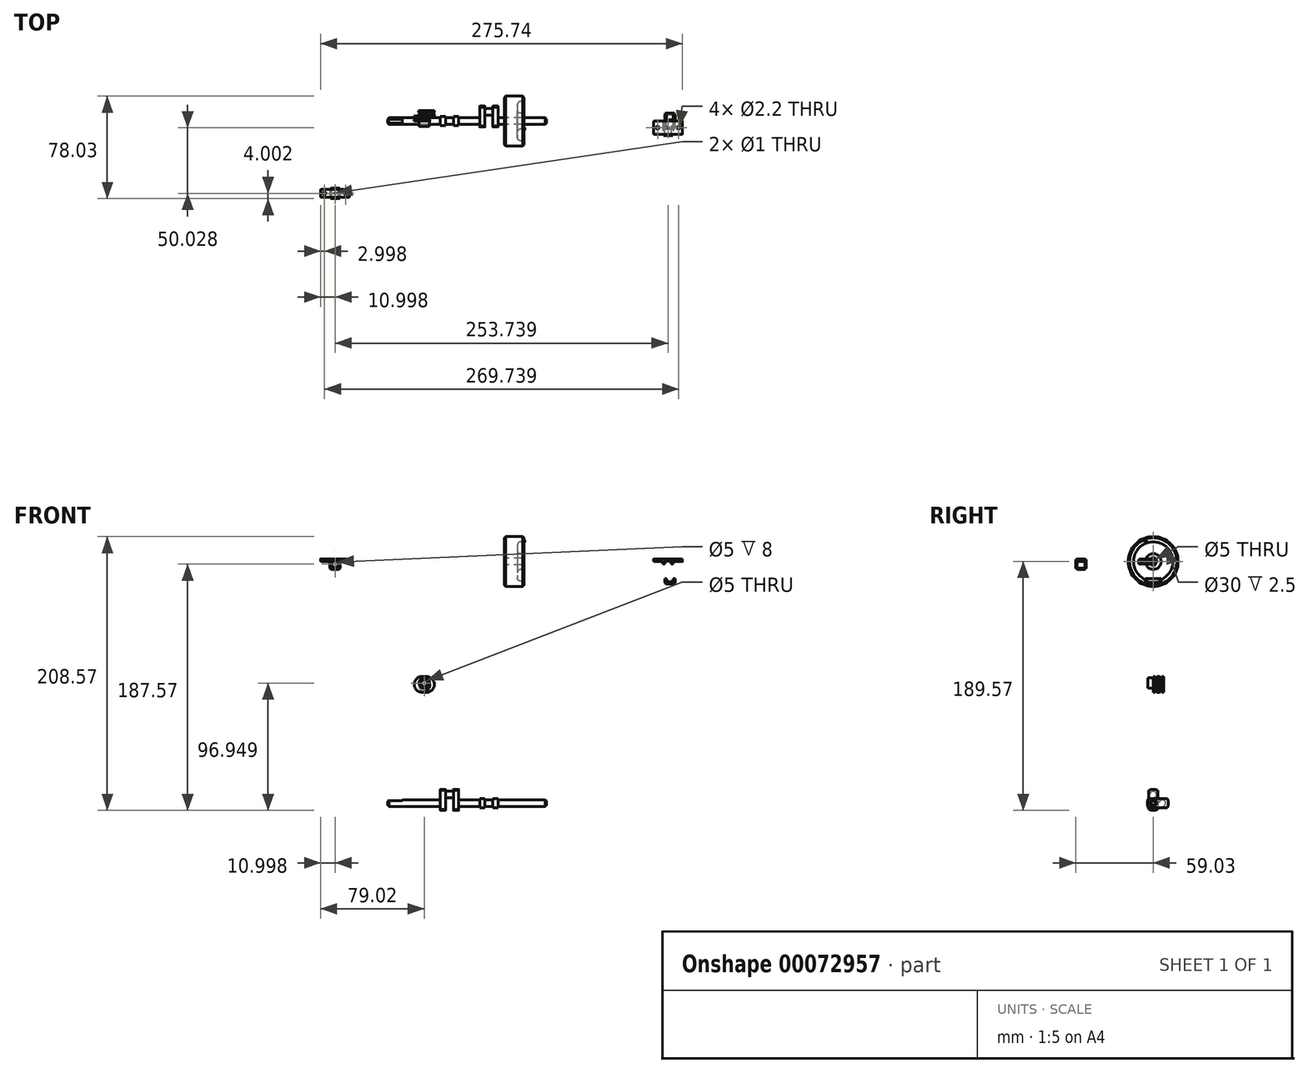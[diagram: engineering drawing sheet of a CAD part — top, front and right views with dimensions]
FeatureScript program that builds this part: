
annotation { "Feature Type Name" : "Feature", "Feature Type Description" : "" }
export const myFeature = defineFeature(function(context is Context, id is Id, definition is map)
    precondition{}
    {
        {
            var Q0;
            Q0=qCreatedBy(makeId("Front.planeOp"),FACE);
            var sketch = newSketch(context, id + "F0", { "sketchPlane" : qUnion([Q0])});
            skLineSegment(sketch, "E0", {"start": v(0, 0) * mm, "end": v(0, 2.5) * mm});
            skLineSegment(sketch, "E1", {"start": v(0, 0) * mm, "end": v(0, 19) * mm});
            skPoint(sketch, "E1.endSnap0", {"position": v(0, 1.25) * mm});
            skLineSegment(sketch, "E2", {"start": v(0, 19) * mm, "end": v(15, 19) * mm});
            skLineSegment(sketch, "E3", {"start": v(0, 19) * mm, "end": v(10, 19) * mm});
            skLineSegment(sketch, "E4", {"start": v(10, 12.5) * mm, "end": v(10, 8.5) * mm});
            skLineSegment(sketch, "E5", {"start": v(12.5, 6) * mm, "end": v(15, 6) * mm});
            skLineSegment(sketch, "E6", {"start": v(15, 19) * mm, "end": v(15, 15) * mm});
            skLineSegment(sketch, "E7", {"start": v(15, 15) * mm, "end": v(12.5, 15) * mm});
            skLineSegment(sketch, "E8", {"start": v(15, 2.5) * mm, "end": v(10, 2.5) * mm});
            skPoint(sketch, "E9.newPointB", {"position": v(10, 0) * mm});
            skArc(sketch, "E9.filletArc", {"start": v(10, 8.5) * mm, "mid": v(10.73, 6.73) * mm, "end": v(12.5, 6) * mm});
            skArc(sketch, "E10.filletArc", {"start": v(12.5, 15) * mm, "mid": v(10.73, 14.27) * mm, "end": v(10, 12.5) * mm});
            skLineSegment(sketch, "E11", {"start": v(15, 6) * mm, "end": v(15, 2.5) * mm});
            skPoint(sketch, "E12.orphan", {"position": v(16.25, 2.5) * mm});
            skLineSegment(sketch, "E13", {"start": v(0, 2.5) * mm, "end": v(15, 2.5) * mm});
            skLineSegment(sketch, "E14", {"start": v(0, 0) * mm, "end": v(10, 0) * mm});
            skSolve(sketch);
        }
        {
            var Q0;
            Q0 = qSketchRegion(id + "F0", true);
            var Q1;
            Q1=sQuery(id+"F0.wireOp",EDGE,"E14");
            revolve(context, id + "F1", {"entities" : qUnion([Q0]), "axis" : qUnion([Q1]), "revolveType" : RevolveType.FULL});
        }
        {
            var Q0;
            Q0=makeQuery(id+"F1.opRevolve","SWEPT_EDGE",EDGE,{"disambiguationData":[OSD([sQuery(id+"F0.wireOp",EDGE,"E2"),sQuery(id+"F0.wireOp",EDGE,"E6")])]});
            chamfer(context, id + "F2", {"entities" : qUnion([Q0]), "width" : 1 * mm, "tangentPropagation" : true});
        }
        {
            var Q0;
            Q0=makeQuery(id+"F1.opRevolve","SWEPT_EDGE",EDGE,{"disambiguationData":[OSD([sQuery(id+"F0.wireOp",EDGE,"E1"),sQuery(id+"F0.wireOp",EDGE,"E3")])]});
            chamfer(context, id + "F3", {"entities" : qUnion([Q0]), "width" : 1 * mm, "tangentPropagation" : true});
        }
        {
            var Q0;
            Q0=qCreatedBy(makeId("Front.planeOp"),FACE);
            var sketch = newSketch(context, id + "F4", { "sketchPlane" : qUnion([Q0])});
            skLineSegment(sketch, "E15", {"start": v(-88.77, -184.07) * mm, "end": v(-48.77, -184.07) * mm});
            skLineSegment(sketch, "E16", {"start": v(-48.77, -184.07) * mm, "end": v(-48.77, -186.57) * mm});
            skLineSegment(sketch, "E17", {"start": v(-48.77, -186.57) * mm, "end": v(-88.77, -186.57) * mm});
            skLineSegment(sketch, "E18", {"start": v(-88.77, -186.57) * mm, "end": v(-88.77, -184.07) * mm});
            skSolve(sketch);
        }
        {
            var Q0;
            Q0=makeQuery(id+"F4.imprint","IMPRINT",FACE,{"disambiguationData":[TD([[makeQuery(id+"F4.imprint","IMPRINT",EDGE,{"derivedFrom":sQuery(id+"F4.wireOp",EDGE,"E15")}),-1.0]])]});
            var Q1;
            Q1=sQuery(id+"F4.wireOp",EDGE,"E15");
            revolve(context, id + "F5", {"entities" : qUnion([Q0]), "axis" : qUnion([Q1]), "revolveType" : RevolveType.FULL});
        }
        {
            var Q0;
            Q0=makeQuery(id+"F5.opRevolve","SWEPT_FACE",FACE,{"disambiguationData":[OSD([sQuery(id+"F4.wireOp",EDGE,"E18")])]});
            var sketch = newSketch(context, id + "F6", { "sketchPlane" : qUnion([Q0])});
            skLineSegment(sketch, "E19", {"start": v(0, -184.07) * mm, "end": v(0, -182.07) * mm});
            skLineSegment(sketch, "E20", {"start": v(0, -182.07) * mm, "end": v(-1.5, -182.07) * mm});
            skLineSegment(sketch, "E21", {"start": v(-1.5, -182.07) * mm, "end": v(1.5, -182.07) * mm});
            skLineSegment(sketch, "E22", {"start": v(1.5, -182.07) * mm, "end": v(1.5, -180.36) * mm});
            skLineSegment(sketch, "E23", {"start": v(1.5, -180.36) * mm, "end": v(-1.5, -180.36) * mm});
            skLineSegment(sketch, "E24", {"start": v(-1.5, -180.36) * mm, "end": v(-1.5, -182.07) * mm});
            skSolve(sketch);
        }
        {
            var Q0;
            Q0 = qSketchRegion(id + "F6", true);
            extrude(context, id + "F7", {"entities" : qUnion([Q0]), "operationType" : NewBodyOperationType.REMOVE, "oppositeDirection" : true, "depth" : 11 * mm});
        }
        {
            var Q0;
            Q0=makeQuery(id+"F5.opRevolve","SWEPT_EDGE",EDGE,{"disambiguationData":[OSD([sQuery(id+"F4.wireOp",EDGE,"E17"),sQuery(id+"F4.wireOp",EDGE,"E18")])]});
            chamfer(context, id + "F8", {"entities" : qUnion([Q0]), "width" : 1 * mm, "tangentPropagation" : true});
        }
        {
            var Q0;
            Q0=makeQuery(id+"F5.opRevolve","SWEPT_FACE",FACE,{"disambiguationData":[OSD([sQuery(id+"F4.wireOp",EDGE,"E16")])]});
            var sketch = newSketch(context, id + "F9", { "sketchPlane" : qUnion([Q0])});
            skLineSegment(sketch, "E25", {"start": v(0, -184.07) * mm, "end": v(0, -177.57) * mm});
            skCircle(sketch, "E26", {"center": v(0, -177.57) * mm, "radius": 2.5 * mm});
            skLineSegment(sketch, "E27", {"start": v(0, -184.07) * mm, "end": v(0, -181.57) * mm});
            skLineSegment(sketch, "E28", {"start": v(0, -181.57) * mm, "end": v(3.5, -181.57) * mm});
            skArc(sketch, "E29", {"start": v(-3.5, -188.76) * mm, "mid": v(0, -189.57) * mm, "end": v(3.5, -188.76) * mm});
            skLineSegment(sketch, "E30", {"start": v(3.5, -181.57) * mm, "end": v(3.5, -184.76) * mm});
            skLineSegment(sketch, "E31", {"start": v(3.5, -184.76) * mm, "end": v(3.5, -188.76) * mm});
            skLineSegment(sketch, "E32", {"start": v(3.5, -188.76) * mm, "end": v(3.5, -174.38) * mm});
            skLineSegment(sketch, "E33.MirrorCS", {"start": v(-3.5, -188.76) * mm, "end": v(-3.5, -174.38) * mm});
            skPoint(sketch, "E34.orphan", {"position": v(3.5, -170.38) * mm});
            skArc(sketch, "E35.trimOffspring", {"start": v(3.5, -174.38) * mm, "mid": v(0, -173.57) * mm, "end": v(-3.5, -174.38) * mm});
            skPoint(sketch, "E36.MirrorCS.end.orphan", {"position": v(-3.5, -170.38) * mm});
            skSolve(sketch);
        }
        {
            var Q0;
            Q0 = qSketchRegion(id + "F9", true);
            var Q1;
            Q1=makeQuery(id+"F9.imprint","IMPRINT",FACE,{"disambiguationData":[TD([[makeQuery(id+"F9.imprint","IMPRINT",EDGE,{"derivedFrom":sQuery(id+"F9.wireOp",EDGE,"E26")}),1.0]])]});
            extrude(context, id + "F10", {"entities" : qUnion([Q0, Q1]), "operationType" : NewBodyOperationType.ADD, "depth" : 4 * mm});
        }
        {
            var Q0;
            Q0=makeQuery(id+"F9.imprint","IMPRINT",FACE,{"disambiguationData":[TD([[makeQuery(id+"F9.imprint","IMPRINT",EDGE,{"derivedFrom":sQuery(id+"F9.wireOp",EDGE,"E26")}),1.0]])]});
            extrude(context, id + "F11", {"entities" : qUnion([Q0]), "operationType" : NewBodyOperationType.ADD, "depth" : 14 * mm});
        }
        {
            var Q0;
            Q0=makeQuery(id+"F11.opExtrude","CAP_FACE",FACE,{"disambiguationData":[OSD([sQuery(id+"F9.wireOp",EDGE,"E26")])],"isStart":false});
            var sketch = newSketch(context, id + "F12", { "sketchPlane" : qUnion([Q0])});
            skLineSegment(sketch, "E37", {"start": v(0, -177.57) * mm, "end": v(0, -184.07) * mm});
            skCircle(sketch, "E38", {"center": v(0, -184.07) * mm, "radius": 2.5 * mm});
            skArc(sketch, "E39", {"start": v(-3.5, -188.76) * mm, "mid": v(0, -189.57) * mm, "end": v(3.5, -188.76) * mm});
            skLineSegment(sketch, "E40", {"start": v(0, -181.57) * mm, "end": v(3.5, -181.57) * mm});
            skLineSegment(sketch, "E41", {"start": v(3.5, -181.57) * mm, "end": v(3.5, -174.38) * mm});
            skLineSegment(sketch, "E42", {"start": v(3.5, -174.38) * mm, "end": v(3.5, -188.76) * mm});
            skLineSegment(sketch, "E43.MirrorCS", {"start": v(-3.5, -174.38) * mm, "end": v(-3.5, -188.76) * mm});
            skArc(sketch, "E44.trimOffspring", {"start": v(3.5, -174.38) * mm, "mid": v(0, -173.57) * mm, "end": v(-3.5, -174.38) * mm});
            skSolve(sketch);
        }
        {
            var Q0;
            Q0 = qSketchRegion(id + "F12", true);
            var Q1;
            Q1=makeQuery(id+"F12.imprint","IMPRINT",FACE,{"disambiguationData":[TD([[makeQuery(id+"F12.imprint","IMPRINT",EDGE,{"derivedFrom":sQuery(id+"F12.wireOp",EDGE,"E38")}),1.0]])]});
            extrude(context, id + "F13", {"entities" : qUnion([Q0, Q1]), "operationType" : NewBodyOperationType.ADD, "oppositeDirection" : true, "depth" : 4 * mm});
        }
        {
            var Q0;
            Q0=makeQuery(id+"F12.imprint","IMPRINT",FACE,{"disambiguationData":[TD([[makeQuery(id+"F12.imprint","IMPRINT",EDGE,{"derivedFrom":sQuery(id+"F12.wireOp",EDGE,"E38")}),1.0]])]});
            extrude(context, id + "F14", {"entities" : qUnion([Q0]), "operationType" : NewBodyOperationType.ADD, "depth" : 16 * mm});
        }
        {
            var Q0;
            Q0=makeQuery(id+"F14.opExtrude","CAP_FACE",FACE,{"disambiguationData":[OSD([sQuery(id+"F12.wireOp",EDGE,"E38")])],"isStart":false});
            var sketch = newSketch(context, id + "F15", { "sketchPlane" : qUnion([Q0])});
            skLineSegment(sketch, "E45", {"start": v(0, -184.07) * mm, "end": v(3.5, -184.07) * mm});
            skArc(sketch, "E46", {"start": v(-3.7, -180.57) * mm, "mid": v(-4.5, -184.07) * mm, "end": v(-3.7, -187.57) * mm});
            skLineSegment(sketch, "E47", {"start": v(3.5, -184.07) * mm, "end": v(3.5, -187.57) * mm});
            skLineSegment(sketch, "E48", {"start": v(3.5, -187.57) * mm, "end": v(10.7, -187.57) * mm});
            skLineSegment(sketch, "E49", {"start": v(10.7, -187.57) * mm, "end": v(-3.7, -187.57) * mm});
            skLineSegment(sketch, "E50.MirrorCS", {"start": v(10.7, -180.57) * mm, "end": v(-3.7, -180.57) * mm});
            skArc(sketch, "E51.trimOffspring", {"start": v(10.7, -187.57) * mm, "mid": v(11.5, -184.07) * mm, "end": v(10.7, -180.57) * mm});
            skCircle(sketch, "E52", {"center": v(0, -184.07) * mm, "radius": 2.5 * mm});
            skSolve(sketch);
        }
        {
            var Q0;
            Q0 = qSketchRegion(id + "F15", true);
            var Q1;
            Q1=makeQuery(id+"F15.imprint","IMPRINT",FACE,{"disambiguationData":[TD([[makeQuery(id+"F15.imprint","IMPRINT",EDGE,{"derivedFrom":sQuery(id+"F15.wireOp",EDGE,"E52")}),1.0]])]});
            extrude(context, id + "F16", {"entities" : qUnion([Q0, Q1]), "operationType" : NewBodyOperationType.ADD, "depth" : 4 * mm});
        }
        {
            var Q0;
            Q0=makeQuery(id+"F16.opExtrude","CAP_FACE",FACE,{"disambiguationData":[OSD([sQuery(id+"F15.wireOp",EDGE,"E46"),sQuery(id+"F15.wireOp",EDGE,"E49"),sQuery(id+"F15.wireOp",EDGE,"E50.MirrorCS"),sQuery(id+"F15.wireOp",EDGE,"E51.trimOffspring")])],"isStart":false});
            var sketch = newSketch(context, id + "F17", { "sketchPlane" : qUnion([Q0])});
            skLineSegment(sketch, "E53", {"start": v(3.5, -187.57) * mm, "end": v(3.5, -184.07) * mm});
            skLineSegment(sketch, "E54", {"start": v(3.5, -184.07) * mm, "end": v(0, -184.07) * mm});
            skCircle(sketch, "E55", {"center": v(0, -184.07) * mm, "radius": 2.5 * mm});
            skCircle(sketch, "E56.MirrorC", {"center": v(7, -184.07) * mm, "radius": 2.5 * mm});
            skSolve(sketch);
        }
        {
            var Q0;
            Q0 = qSketchRegion(id + "F17", true);
            extrude(context, id + "F18", {"entities" : qUnion([Q0]), "operationType" : NewBodyOperationType.ADD, "depth" : 6 * mm});
        }
        {
            var Q0;
            Q0=makeQuery(id+"F18.opExtrude","CAP_FACE",FACE,{"disambiguationData":[OSD([sQuery(id+"F17.wireOp",EDGE,"E55")])],"isStart":false});
            var sketch = newSketch(context, id + "F19", { "sketchPlane" : qUnion([Q0])});
            skLineSegment(sketch, "E57", {"start": v(0, -184.07) * mm, "end": v(3.5, -184.07) * mm});
            skArc(sketch, "E58", {"start": v(-3.7, -180.57) * mm, "mid": v(-4.5, -184.07) * mm, "end": v(-3.7, -187.57) * mm});
            skLineSegment(sketch, "E59", {"start": v(3.5, -184.07) * mm, "end": v(3.5, -180.57) * mm});
            skLineSegment(sketch, "E60", {"start": v(3.5, -180.57) * mm, "end": v(-3.7, -180.57) * mm});
            skLineSegment(sketch, "E61", {"start": v(-3.7, -180.57) * mm, "end": v(10.7, -180.57) * mm});
            skLineSegment(sketch, "E62.MirrorCS", {"start": v(-3.7, -187.57) * mm, "end": v(10.7, -187.57) * mm});
            skArc(sketch, "E63.trimOffspring", {"start": v(10.7, -187.57) * mm, "mid": v(11.5, -184.07) * mm, "end": v(10.7, -180.57) * mm});
            skSolve(sketch);
        }
        {
            var Q0;
            Q0 = qSketchRegion(id + "F19", true);
            extrude(context, id + "F20", {"entities" : qUnion([Q0]), "operationType" : NewBodyOperationType.ADD, "depth" : 4 * mm});
        }
        {
            var Q0;
            Q0=makeQuery(id+"F20.opExtrude","CAP_FACE",FACE,{"disambiguationData":[OSD([sQuery(id+"F19.wireOp",EDGE,"E58"),sQuery(id+"F19.wireOp",EDGE,"E61"),sQuery(id+"F19.wireOp",EDGE,"E62.MirrorCS"),sQuery(id+"F19.wireOp",EDGE,"E63.trimOffspring")])],"isStart":false});
            var sketch = newSketch(context, id + "F21", { "sketchPlane" : qUnion([Q0])});
            skLineSegment(sketch, "E64", {"start": v(3.5, -187.57) * mm, "end": v(3.5, -184.07) * mm});
            skLineSegment(sketch, "E65", {"start": v(3.5, -184.07) * mm, "end": v(0, -184.07) * mm});
            skCircle(sketch, "E66", {"center": v(0, -184.07) * mm, "radius": 2.5 * mm});
            skSolve(sketch);
        }
        {
            var Q0;
            Q0 = qSketchRegion(id + "F21", true);
            extrude(context, id + "F22", {"entities" : qUnion([Q0]), "operationType" : NewBodyOperationType.ADD, "depth" : 37 * mm});
        }
        {
            var Q0;
            Q0=makeQuery(id+"F22.opExtrude","CAP_EDGE",EDGE,{"disambiguationData":[OSD([sQuery(id+"F21.wireOp",EDGE,"E66")])],"isStart":false});
            chamfer(context, id + "F23", {"entities" : qUnion([Q0]), "width" : 1 * mm, "tangentPropagation" : true});
        }
        {
            var Q0;
            Q0=qCreatedBy(makeId("Top.planeOp"),FACE);
            var sketch = newSketch(context, id + "F24", { "sketchPlane" : qUnion([Q0])});
            skLineSegment(sketch, "E67", {"start": v(113.76, -9.5) * mm, "end": v(113.76, -0.5) * mm});
            skLineSegment(sketch, "E68", {"start": v(114.26, 0) * mm, "end": v(135.26, 0) * mm});
            skLineSegment(sketch, "E69", {"start": v(135.76, -0.5) * mm, "end": v(135.76, -9.5) * mm});
            skLineSegment(sketch, "E70", {"start": v(135.26, -10) * mm, "end": v(114.26, -10) * mm});
            skLineSegment(sketch, "E71", {"start": v(124.76, -10) * mm, "end": v(116.76, -10) * mm});
            skLineSegment(sketch, "E72", {"start": v(116.76, -10) * mm, "end": v(116.76, -5) * mm});
            skPoint(sketch, "E72.endSnap0", {"position": v(113.76, -5) * mm});
            skCircle(sketch, "E73", {"center": v(116.76, -5) * mm, "radius": 1.1 * mm});
            skLineSegment(sketch, "E74", {"start": v(124.76, 0) * mm, "end": v(124.76, -1.07) * mm});
            skCircle(sketch, "E75.MirrorC", {"center": v(132.76, -5) * mm, "radius": 1.1 * mm});
            skLineSegment(sketch, "E76", {"start": v(124.76, -5) * mm, "end": v(125.26, -5) * mm});
            skCircle(sketch, "E77", {"center": v(124.76, -5) * mm, "radius": 0.5 * mm});
            skPoint(sketch, "E78.visualSharp", {"position": v(113.76, 0) * mm});
            skArc(sketch, "E78.filletArc", {"start": v(114.26, 0) * mm, "mid": v(113.9, -0.15) * mm, "end": v(113.76, -0.5) * mm});
            skPoint(sketch, "E79.visualSharp", {"position": v(113.76, -10) * mm});
            skArc(sketch, "E79.filletArc", {"start": v(113.76, -9.5) * mm, "mid": v(113.9, -9.85) * mm, "end": v(114.26, -10) * mm});
            skPoint(sketch, "E80.visualSharp", {"position": v(135.76, -10) * mm});
            skArc(sketch, "E80.filletArc", {"start": v(135.26, -10) * mm, "mid": v(135.61, -9.85) * mm, "end": v(135.76, -9.5) * mm});
            skPoint(sketch, "E81.visualSharp", {"position": v(135.76, 0) * mm});
            skArc(sketch, "E81.filletArc", {"start": v(135.76, -0.5) * mm, "mid": v(135.61, -0.15) * mm, "end": v(135.26, 0) * mm});
            skSolve(sketch);
        }
        {
            var Q0;
            Q0=makeQuery(id+"F24.imprint","IMPRINT",FACE,{"disambiguationData":[TD([[makeQuery(id+"F24.imprint","IMPRINT",EDGE,{"derivedFrom":sQuery(id+"F24.wireOp",EDGE,"E67")}),-1.0]])]});
            extrude(context, id + "F25", {"entities" : qUnion([Q0]), "depth" : 2 * mm});
        }
        {
            var Q0;
            Q0=makeQuery(id+"F25.opExtrude","SWEPT_FACE",FACE,{"disambiguationData":[OSD([sQuery(id+"F24.wireOp",EDGE,"E70"),sQuery(id+"F24.wireOp",EDGE,"E71")])]});
            var sketch = newSketch(context, id + "F26", { "sketchPlane" : qUnion([Q0])});
            skLineSegment(sketch, "E82", {"start": v(124.76, 0) * mm, "end": v(124.76, -2) * mm});
            skArc(sketch, "E83", {"start": v(128.26, -2) * mm, "mid": v(124.76, 1.5) * mm, "end": v(121.26, -2) * mm});
            skArc(sketch, "E84", {"start": v(127.26, -2) * mm, "mid": v(124.76, 0.5) * mm, "end": v(122.26, -2) * mm});
            skLineSegment(sketch, "E85", {"start": v(124.76, -2) * mm, "end": v(128.26, -2) * mm});
            skLineSegment(sketch, "E86", {"start": v(128.26, -2) * mm, "end": v(127.26, -2) * mm});
            skLineSegment(sketch, "E87.trimOffspring", {"start": v(122.26, -2) * mm, "end": v(121.26, -2) * mm});
            skSolve(sketch);
        }
        {
            var Q0;
            Q0 = qSketchRegion(id + "F26", true);
            extrude(context, id + "F27", {"entities" : qUnion([Q0]), "operationType" : NewBodyOperationType.ADD, "depth" : 1 * mm, "hasSecondDirection" : true, "secondDirectionOppositeDirection" : true, "secondDirectionDepth" : 11 * mm});
        }
        {
            var Q0;
            {var subQ2=sQuery(id+"F24.wireOp",EDGE,"E79.filletArc");var subQ7=sQuery(id+"F24.wireOp",EDGE,"E71");var subQ8=sQuery(id+"F24.wireOp",EDGE,"E70");Q0=makeQuery(id+"F27.boolean.opBoolean","SPLIT",FACE,{"disambiguationData":[TD([makeQuery(id+"F25.opExtrude","SWEPT_FACE",FACE,{"disambiguationData":[OSD([subQ2])]})])],"derivedFrom":makeQuery(id+"F25.opExtrude","SWEPT_FACE",FACE,{"disambiguationData":[OSD([subQ8,subQ7])]})});}
            var sketch = newSketch(context, id + "F28", { "sketchPlane" : qUnion([Q0])});
            skLineSegment(sketch, "E88", {"start": v(135.26, 0) * mm, "end": v(114.26, 0) * mm});
            skLineSegment(sketch, "E89", {"start": v(114.26, 0) * mm, "end": v(124.76, 0) * mm});
            skLineSegment(sketch, "E90", {"start": v(124.76, 0) * mm, "end": v(124.76, -2) * mm});
            skLineSegment(sketch, "E91", {"start": v(124.76, -2) * mm, "end": v(128.76, -2) * mm});
            skLineSegment(sketch, "E92", {"start": v(128.76, -2) * mm, "end": v(128.76, 0) * mm});
            skLineSegment(sketch, "E93", {"start": v(128.76, 0) * mm, "end": v(127.63, 0) * mm});
            skLineSegment(sketch, "E94.MirrorCS", {"start": v(124.76, -2) * mm, "end": v(120.76, -2) * mm});
            skLineSegment(sketch, "E95.MirrorCS", {"start": v(120.76, -2) * mm, "end": v(120.76, 0) * mm});
            skLineSegment(sketch, "E96.MirrorCS", {"start": v(120.76, 0) * mm, "end": v(121.89, 0) * mm});
            skSolve(sketch);
        }
        {
            var Q0;
            Q0 = qSketchRegion(id + "F28", true);
            extrude(context, id + "F29", {"entities" : qUnion([Q0]), "operationType" : NewBodyOperationType.ADD, "oppositeDirection" : true, "depth" : 10 * mm});
        }
        {
            var Q0;
            {var subQ0=sQuery(id+"F24.wireOp",EDGE,"E71");var subQ1=sQuery(id+"F24.wireOp",EDGE,"E70");Q0=makeQuery(id+"F29.boolean.opBoolean","MERGE",FACE,{"derivedFrom":[makeQuery(id+"F27.boolean.opBoolean","SPLIT",FACE,{"disambiguationData":[TD([makeQuery(id+"F27.opExtrude","SWEPT_FACE",FACE,{"disambiguationData":[OSD([sQuery(id+"F26.wireOp",EDGE,"E84")])]})])],"derivedFrom":makeQuery(id+"F25.opExtrude","SWEPT_FACE",FACE,{"disambiguationData":[OSD([subQ1,subQ0])]})}),makeQuery(id+"F29.opExtrude","CAP_FACE",FACE,{"disambiguationData":[OSD([sQuery(id+"F28.wireOp",EDGE,"E88"),sQuery(id+"F28.wireOp",EDGE,"E89"),sQuery(id+"F28.wireOp",EDGE,"E91"),sQuery(id+"F28.wireOp",EDGE,"E92"),sQuery(id+"F28.wireOp",EDGE,"E93"),sQuery(id+"F28.wireOp",EDGE,"E94.MirrorCS"),sQuery(id+"F28.wireOp",EDGE,"E95.MirrorCS"),sQuery(id+"F28.wireOp",EDGE,"E96.MirrorCS")])],"isStart":true})]});}
            var sketch = newSketch(context, id + "F30", { "sketchPlane" : qUnion([Q0])});
            skCircle(sketch, "E97", {"center": v(124.76, -2) * mm, "radius": 2.5 * mm});
            skSolve(sketch);
        }
        {
            var Q0;
            Q0 = qSketchRegion(id + "F30", true);
            extrude(context, id + "F31", {"entities" : qUnion([Q0]), "operationType" : NewBodyOperationType.REMOVE, "oppositeDirection" : true, "depth" : 25 * mm});
        }
        {
            var Q0;
            Q0=qCreatedBy(makeId("Front.planeOp"),FACE);
            var sketch = newSketch(context, id + "F32", { "sketchPlane" : qUnion([Q0])});
            skLineSegment(sketch, "E98.bottom", {"start": v(122.14, -13.08) * mm, "end": v(126.14, -13.08) * mm});
            skLineSegment(sketch, "E98.top", {"start": v(122.14, -17.08) * mm, "end": v(130.14, -17.08) * mm});
            skLineSegment(sketch, "E98.left", {"start": v(122.14, -13.08) * mm, "end": v(122.14, -17.08) * mm});
            skLineSegment(sketch, "E98.right", {"start": v(130.14, -13.08) * mm, "end": v(130.14, -17.08) * mm});
            skArc(sketch, "E99", {"start": v(122.64, -13.08) * mm, "mid": v(126.14, -16.58) * mm, "end": v(129.64, -13.08) * mm});
            skArc(sketch, "E100", {"start": v(123.64, -13.08) * mm, "mid": v(126.14, -15.58) * mm, "end": v(128.64, -13.08) * mm});
            skLineSegment(sketch, "E101.trimOffspring", {"start": v(128.64, -13.08) * mm, "end": v(130.14, -13.08) * mm});
            skSolve(sketch);
        }
        {
            var Q0;
            Q0 = qSketchRegion(id + "F32", true);
            extrude(context, id + "F33", {"entities" : qUnion([Q0]), "endBound" : BoundingType.SYMMETRIC, "depth" : 10 * mm});
        }
        {
            var Q0;
            {var subQ0=sQuery(id+"F32.wireOp",EDGE,"E99");Q0=makeQuery(id+"F32.imprint","IMPRINT",FACE,{"disambiguationData":[TD([[makeQuery(id+"F32.imprint","IMPRINT",EDGE,{"derivedFrom":subQ0}),1.0]])]});}
            extrude(context, id + "F34", {"entities" : qUnion([Q0]), "operationType" : NewBodyOperationType.ADD, "endBound" : BoundingType.SYMMETRIC, "depth" : 12 * mm});
        }
        {
            var Q0;
            Q0=makeQuery(id+"F33.opExtrude","SWEPT_EDGE",EDGE,{"disambiguationData":[OSD([sQuery(id+"F32.wireOp",EDGE,"E98.top"),sQuery(id+"F32.wireOp",EDGE,"E98.left")])]});
            var Q1;
            Q1=makeQuery(id+"F33.opExtrude","SWEPT_EDGE",EDGE,{"disambiguationData":[OSD([sQuery(id+"F32.wireOp",EDGE,"E98.top"),sQuery(id+"F32.wireOp",EDGE,"E98.right")])]});
            chamfer(context, id + "F35", {"entities" : qUnion([Q0, Q1]), "width" : 1 * mm, "tangentPropagation" : true});
        }
        {
            var Q0;
            Q0=qCreatedBy(makeId("Top.planeOp"),FACE);
            var sketch = newSketch(context, id + "F36", { "sketchPlane" : qUnion([Q0])});
            skLineSegment(sketch, "E102.bottom", {"start": v(-139.48, -52.03) * mm, "end": v(-118.48, -52.03) * mm});
            skLineSegment(sketch, "E102.top", {"start": v(-139.48, -58.03) * mm, "end": v(-118.48, -58.03) * mm});
            skLineSegment(sketch, "E102.left", {"start": v(-139.98, -52.53) * mm, "end": v(-139.98, -57.53) * mm});
            skLineSegment(sketch, "E102.right", {"start": v(-117.98, -52.53) * mm, "end": v(-117.98, -57.53) * mm});
            skLineSegment(sketch, "E103", {"start": v(-128.98, -55.03) * mm, "end": v(-136.98, -55.03) * mm});
            skPoint(sketch, "E103.startSnap0", {"position": v(-139.98, -55.03) * mm});
            skPoint(sketch, "E103.startSnap1", {"position": v(-128.98, -52.03) * mm});
            skCircle(sketch, "E104", {"center": v(-136.98, -55.03) * mm, "radius": 1.1 * mm});
            skLineSegment(sketch, "E105", {"start": v(-128.98, -52.03) * mm, "end": v(-128.98, -51.12) * mm});
            skCircle(sketch, "E106.MirrorC", {"center": v(-120.98, -55.03) * mm, "radius": 1.1 * mm});
            skCircle(sketch, "E107", {"center": v(-128.98, -55.03) * mm, "radius": 0.5 * mm});
            skPoint(sketch, "E108.visualSharp", {"position": v(-139.98, -52.03) * mm});
            skArc(sketch, "E108.filletArc", {"start": v(-139.48, -52.03) * mm, "mid": v(-139.84, -52.17) * mm, "end": v(-139.98, -52.53) * mm});
            skPoint(sketch, "E109.visualSharp", {"position": v(-139.98, -58.03) * mm});
            skArc(sketch, "E109.filletArc", {"start": v(-139.98, -57.53) * mm, "mid": v(-139.84, -57.88) * mm, "end": v(-139.48, -58.03) * mm});
            skPoint(sketch, "E110.visualSharp", {"position": v(-117.98, -58.03) * mm});
            skArc(sketch, "E110.filletArc", {"start": v(-118.48, -58.03) * mm, "mid": v(-118.13, -57.88) * mm, "end": v(-117.98, -57.53) * mm});
            skPoint(sketch, "E111.visualSharp", {"position": v(-117.98, -52.03) * mm});
            skArc(sketch, "E111.filletArc", {"start": v(-117.98, -52.53) * mm, "mid": v(-118.13, -52.17) * mm, "end": v(-118.48, -52.03) * mm});
            skSolve(sketch);
        }
        {
            var Q0;
            Q0 = qSketchRegion(id + "F36", true);
            extrude(context, id + "F37", {"entities" : qUnion([Q0]), "depth" : 2 * mm});
        }
        {
            var Q0;
            Q0=makeQuery(id+"F37.opExtrude","SWEPT_FACE",FACE,{"disambiguationData":[OSD([sQuery(id+"F36.wireOp",EDGE,"E102.top")])]});
            var sketch = newSketch(context, id + "F38", { "sketchPlane" : qUnion([Q0])});
            skLineSegment(sketch, "E112", {"start": v(-128.98, 0) * mm, "end": v(-128.98, -6) * mm});
            skLineSegment(sketch, "E113", {"start": v(-128.98, -6) * mm, "end": v(-132.98, -6) * mm});
            skLineSegment(sketch, "E114", {"start": v(-132.98, -6) * mm, "end": v(-132.98, 0) * mm});
            skLineSegment(sketch, "E115.MirrorCS", {"start": v(-124.98, -6) * mm, "end": v(-124.98, 0) * mm});
            skLineSegment(sketch, "E116.MirrorCS", {"start": v(-128.98, -6) * mm, "end": v(-124.98, -6) * mm});
            skLineSegment(sketch, "E117", {"start": v(-132.98, 0) * mm, "end": v(-132.98, 2) * mm});
            skLineSegment(sketch, "E118", {"start": v(-132.98, 2) * mm, "end": v(-132.98, -6) * mm});
            skLineSegment(sketch, "E119", {"start": v(-128.98, -6) * mm, "end": v(-128.98, 2) * mm});
            skCircle(sketch, "E120", {"center": v(-128.98, -2) * mm, "radius": 3.5 * mm});
            skCircle(sketch, "E121", {"center": v(-128.98, -2) * mm, "radius": 2.5 * mm});
            skSolve(sketch);
        }
        {
            var Q0;
            {var subQ5=sQuery(id+"F38.wireOp",EDGE,"E113");Q0=makeQuery(id+"F38.imprint","IMPRINT",FACE,{"disambiguationData":[TD([[makeQuery(id+"F38.imprint","IMPRINT",EDGE,{"derivedFrom":subQ5}),-1.0]])]});}
            var Q1;
            {var subQ6=sQuery(id+"F38.wireOp",EDGE,"E115.MirrorCS");Q1=makeQuery(id+"F38.imprint","IMPRINT",FACE,{"disambiguationData":[TD([[makeQuery(id+"F38.imprint","IMPRINT",EDGE,{"derivedFrom":subQ6}),1.0]])]});}
            extrude(context, id + "F39", {"entities" : qUnion([Q0, Q1]), "operationType" : NewBodyOperationType.ADD, "oppositeDirection" : true, "depth" : 6 * mm});
        }
        {
            var Q0;
            {var subQ0=sQuery(id+"F36.wireOp",EDGE,"E102.top");Q0=makeQuery(id+"F39.boolean.opBoolean","MERGE",FACE,{"derivedFrom":[makeQuery(id+"F37.opExtrude","SWEPT_FACE",FACE,{"disambiguationData":[OSD([subQ0])]}),makeQuery(id+"F39.opExtrude","CAP_FACE",FACE,{"disambiguationData":[OSD([subQ0,sQuery(id+"F38.wireOp",EDGE,"E113"),sQuery(id+"F38.wireOp",EDGE,"E115.MirrorCS"),sQuery(id+"F38.wireOp",EDGE,"E116.MirrorCS"),sQuery(id+"F38.wireOp",EDGE,"E118"),sQuery(id+"F38.wireOp",EDGE,"E120")])],"isStart":true})]});}
            var sketch = newSketch(context, id + "F40", { "sketchPlane" : qUnion([Q0])});
            skLineSegment(sketch, "E122", {"start": v(-128.98, 0) * mm, "end": v(-128.98, -2) * mm});
            skCircle(sketch, "E123", {"center": v(-128.98, -2) * mm, "radius": 3.5 * mm});
            skCircle(sketch, "E124", {"center": v(-128.98, -2) * mm, "radius": 2.5 * mm});
            skSolve(sketch);
        }
        {
            var Q0;
            Q0 = qSketchRegion(id + "F40", true);
            extrude(context, id + "F41", {"entities" : qUnion([Q0]), "operationType" : NewBodyOperationType.ADD, "depth" : 1 * mm, "hasSecondDirection" : true, "secondDirectionOppositeDirection" : true, "secondDirectionDepth" : 7 * mm});
        }
        {
            var Q0;
            {var subQ0=sQuery(id+"F36.wireOp",EDGE,"E102.top");Q0=makeQuery(id+"F41.boolean.opBoolean","SPLIT",FACE,{"disambiguationData":[TD([makeQuery(id+"F41.opExtrude","SWEPT_FACE",FACE,{"disambiguationData":[OSD([sQuery(id+"F40.wireOp",EDGE,"E124")])]})])],"derivedFrom":makeQuery(id+"F39.boolean.opBoolean","MERGE",FACE,{"derivedFrom":[makeQuery(id+"F37.opExtrude","SWEPT_FACE",FACE,{"disambiguationData":[OSD([subQ0])]}),makeQuery(id+"F39.opExtrude","CAP_FACE",FACE,{"disambiguationData":[OSD([subQ0,sQuery(id+"F38.wireOp",EDGE,"E113"),sQuery(id+"F38.wireOp",EDGE,"E115.MirrorCS"),sQuery(id+"F38.wireOp",EDGE,"E116.MirrorCS"),sQuery(id+"F38.wireOp",EDGE,"E118"),sQuery(id+"F38.wireOp",EDGE,"E120")])],"isStart":true})]})});}
            var sketch = newSketch(context, id + "F42", { "sketchPlane" : qUnion([Q0])});
            skCircle(sketch, "E125", {"center": v(-128.98, -2) * mm, "radius": 2.5 * mm});
            skSolve(sketch);
        }
        {
            var Q0;
            Q0 = qSketchRegion(id + "F42", true);
            extrude(context, id + "F43", {"entities" : qUnion([Q0]), "operationType" : NewBodyOperationType.REMOVE, "oppositeDirection" : true, "depth" : 25 * mm});
        }
        {
            var Q0;
            Q0=makeQuery(id+"F39.opExtrude","SWEPT_EDGE",EDGE,{"disambiguationData":[OSD([sQuery(id+"F38.wireOp",EDGE,"E113"),sQuery(id+"F38.wireOp",EDGE,"E118")])]});
            var Q1;
            Q1=makeQuery(id+"F39.opExtrude","SWEPT_EDGE",EDGE,{"disambiguationData":[OSD([sQuery(id+"F38.wireOp",EDGE,"E115.MirrorCS"),sQuery(id+"F38.wireOp",EDGE,"E116.MirrorCS")])]});
            chamfer(context, id + "F44", {"entities" : qUnion([Q0, Q1]), "width" : 1 * mm, "tangentPropagation" : true});
        }
        {
            var Q0;
            Q0=qCreatedBy(makeId("Front.planeOp"),FACE);
            var sketch = newSketch(context, id + "F45", { "sketchPlane" : qUnion([Q0])});
            skCircle(sketch, "E126", {"center": v(-60.96, -92.62) * mm, "radius": 4 * mm});
            skSolve(sketch);
        }
        {
            var Q0;
            Q0 = qSketchRegion(id + "F45", true);
            extrude(context, id + "F46", {"entities" : qUnion([Q0]), "depth" : 4 * mm});
        }
        {
            var Q0;
            Q0=makeQuery(id+"F46.opExtrude","CAP_FACE",FACE,{"disambiguationData":[OSD([sQuery(id+"F45.wireOp",EDGE,"E126")])],"isStart":true});
            var sketch = newSketch(context, id + "F47", { "sketchPlane" : qUnion([Q0])});
            skLineSegment(sketch, "E127", {"start": v(60.96, -92.62) * mm, "end": v(63.07, -92.62) * mm});
            skLineSegment(sketch, "E128", {"start": v(60.96, -92.62) * mm, "end": v(62.7, -93.62) * mm});
            skCircle(sketch, "E129", {"center": v(62.7, -93.62) * mm, "radius": 6 * mm});
            skSolve(sketch);
        }
        {
            var Q0;
            Q0 = qSketchRegion(id + "F47", true);
            extrude(context, id + "F48", {"entities" : qUnion([Q0]), "operationType" : NewBodyOperationType.ADD, "depth" : 1.2 * mm});
        }
        {
            var Q0;
            Q0=makeQuery(id+"F48.opExtrude","CAP_FACE",FACE,{"disambiguationData":[OSD([sQuery(id+"F47.wireOp",EDGE,"E129")])],"isStart":false});
            var sketch = newSketch(context, id + "F49", { "sketchPlane" : qUnion([Q0])});
            skCircle(sketch, "E130", {"center": v(62.7, -93.62) * mm, "radius": 5.5 * mm});
            skSolve(sketch);
        }
        {
            var Q0;
            Q0 = qSketchRegion(id + "F49", true);
            extrude(context, id + "F50", {"entities" : qUnion([Q0]), "operationType" : NewBodyOperationType.ADD, "depth" : 1.6 * mm});
        }
        {
            var Q0;
            Q0=makeQuery(id+"F50.opExtrude","CAP_FACE",FACE,{"disambiguationData":[OSD([sQuery(id+"F49.wireOp",EDGE,"E130")])],"isStart":false});
            var sketch = newSketch(context, id + "F51", { "sketchPlane" : qUnion([Q0])});
            skCircle(sketch, "E131", {"center": v(62.7, -93.62) * mm, "radius": 6 * mm});
            skSolve(sketch);
        }
        {
            var Q0;
            Q0 = qSketchRegion(id + "F51", true);
            extrude(context, id + "F52", {"entities" : qUnion([Q0]), "operationType" : NewBodyOperationType.ADD, "depth" : 1.2 * mm});
        }
        {
            var Q0;
            Q0=makeQuery(id+"F52.opExtrude","CAP_FACE",FACE,{"disambiguationData":[OSD([sQuery(id+"F51.wireOp",EDGE,"E131")])],"isStart":false});
            var sketch = newSketch(context, id + "F53", { "sketchPlane" : qUnion([Q0])});
            skLineSegment(sketch, "E132", {"start": v(62.7, -93.62) * mm, "end": v(62.7, -87.62) * mm});
            skLineSegment(sketch, "E133", {"start": v(62.7, -93.62) * mm, "end": v(57.5, -90.62) * mm});
            skLineSegment(sketch, "E134", {"start": v(62.7, -93.62) * mm, "end": v(60.96, -92.62) * mm});
            skLineSegment(sketch, "E135", {"start": v(60.96, -92.62) * mm, "end": v(60.96, -91.37) * mm});
            skLineSegment(sketch, "E136.MirrorCS", {"start": v(59.23, -93.62) * mm, "end": v(64.42, -90.62) * mm});
            skCircle(sketch, "E137", {"center": v(59.23, -93.62) * mm, "radius": 6 * mm});
            skSolve(sketch);
        }
        {
            var Q0;
            Q0 = qSketchRegion(id + "F53", true);
            var Q1;
            {var subQ0=sQuery(id+"F53.wireOp",EDGE,"E134");Q1=makeQuery(id+"F53.imprint","IMPRINT",FACE,{"disambiguationData":[TD([[makeQuery(id+"F53.imprint","IMPRINT",EDGE,{"derivedFrom":subQ0}),-1.0]])]});}
            extrude(context, id + "F54", {"entities" : qUnion([Q0, Q1]), "operationType" : NewBodyOperationType.ADD, "depth" : 1.2 * mm});
        }
        {
            var Q0;
            Q0=makeQuery(id+"F54.opExtrude","CAP_FACE",FACE,{"disambiguationData":[OSD([sQuery(id+"F53.wireOp",EDGE,"E137")])],"isStart":false});
            var sketch = newSketch(context, id + "F55", { "sketchPlane" : qUnion([Q0])});
            skCircle(sketch, "E138", {"center": v(59.23, -93.62) * mm, "radius": 5.5 * mm});
            skSolve(sketch);
        }
        {
            var Q0;
            Q0 = qSketchRegion(id + "F55", true);
            extrude(context, id + "F56", {"entities" : qUnion([Q0]), "operationType" : NewBodyOperationType.ADD, "depth" : 1.6 * mm});
        }
        {
            var Q0;
            Q0=makeQuery(id+"F56.opExtrude","CAP_FACE",FACE,{"disambiguationData":[OSD([sQuery(id+"F55.wireOp",EDGE,"E138")])],"isStart":false});
            var sketch = newSketch(context, id + "F57", { "sketchPlane" : qUnion([Q0])});
            skCircle(sketch, "E139", {"center": v(59.23, -93.62) * mm, "radius": 6 * mm});
            skSolve(sketch);
        }
        {
            var Q0;
            Q0 = qSketchRegion(id + "F57", true);
            extrude(context, id + "F58", {"entities" : qUnion([Q0]), "operationType" : NewBodyOperationType.ADD, "depth" : 1.2 * mm});
        }
        {
            var Q0;
            Q0=makeQuery(id+"F46.opExtrude","CAP_FACE",FACE,{"disambiguationData":[OSD([sQuery(id+"F45.wireOp",EDGE,"E126")])],"isStart":false});
            var sketch = newSketch(context, id + "F59", { "sketchPlane" : qUnion([Q0])});
            skCircle(sketch, "E140", {"center": v(-60.96, -92.62) * mm, "radius": 2.5 * mm});
            skSolve(sketch);
        }
        {
            var Q0;
            Q0 = qSketchRegion(id + "F59", true);
            extrude(context, id + "F60", {"entities" : qUnion([Q0]), "operationType" : NewBodyOperationType.REMOVE, "oppositeDirection" : true, "depth" : 25 * mm});
        }
        {
            var Q0;
            Q0=makeQuery(id+"F20.opExtrude","CAP_FACE",FACE,{"disambiguationData":[OSD([sQuery(id+"F19.wireOp",EDGE,"E58"),sQuery(id+"F19.wireOp",EDGE,"E61"),sQuery(id+"F19.wireOp",EDGE,"E62.MirrorCS"),sQuery(id+"F19.wireOp",EDGE,"E63.trimOffspring")])],"isStart":true});
            var sketch = newSketch(context, id + "F61", { "sketchPlane" : qUnion([Q0])});
            skCircle(sketch, "E141", {"center": v(0, -184.07) * mm, "radius": 2.5 * mm});
            skSolve(sketch);
        }
        {
            var Q0;
            Q0 = qSketchRegion(id + "F61", true);
            extrude(context, id + "F62", {"entities" : qUnion([Q0]), "operationType" : NewBodyOperationType.REMOVE, "depth" : 6 * mm});
        }
        {
            var Q0;
            Q0=makeQuery(id+"F1.opRevolve","SWEPT_FACE",FACE,{"disambiguationData":[OSD([sQuery(id+"F0.wireOp",EDGE,"E6")])]});
            var sketch = newSketch(context, id + "F63", { "sketchPlane" : qUnion([Q0])});
            skCircle(sketch, "E142", {"center": v(-5.92, 15.5) * mm, "radius": 0.82 * mm});
            skSolve(sketch);
        }
        {
            var Q0;
            Q0=makeQuery(id+"F63.imprint","IMPRINT",FACE,{"disambiguationData":[TD([[makeQuery(id+"F63.imprint","IMPRINT",EDGE,{"derivedFrom":sQuery(id+"F63.wireOp",EDGE,"E142")}),1.0]])]});
            extrude(context, id + "F64", {"entities" : qUnion([Q0]), "operationType" : NewBodyOperationType.ADD, "depth" : .5 * mm});
        }
    });
